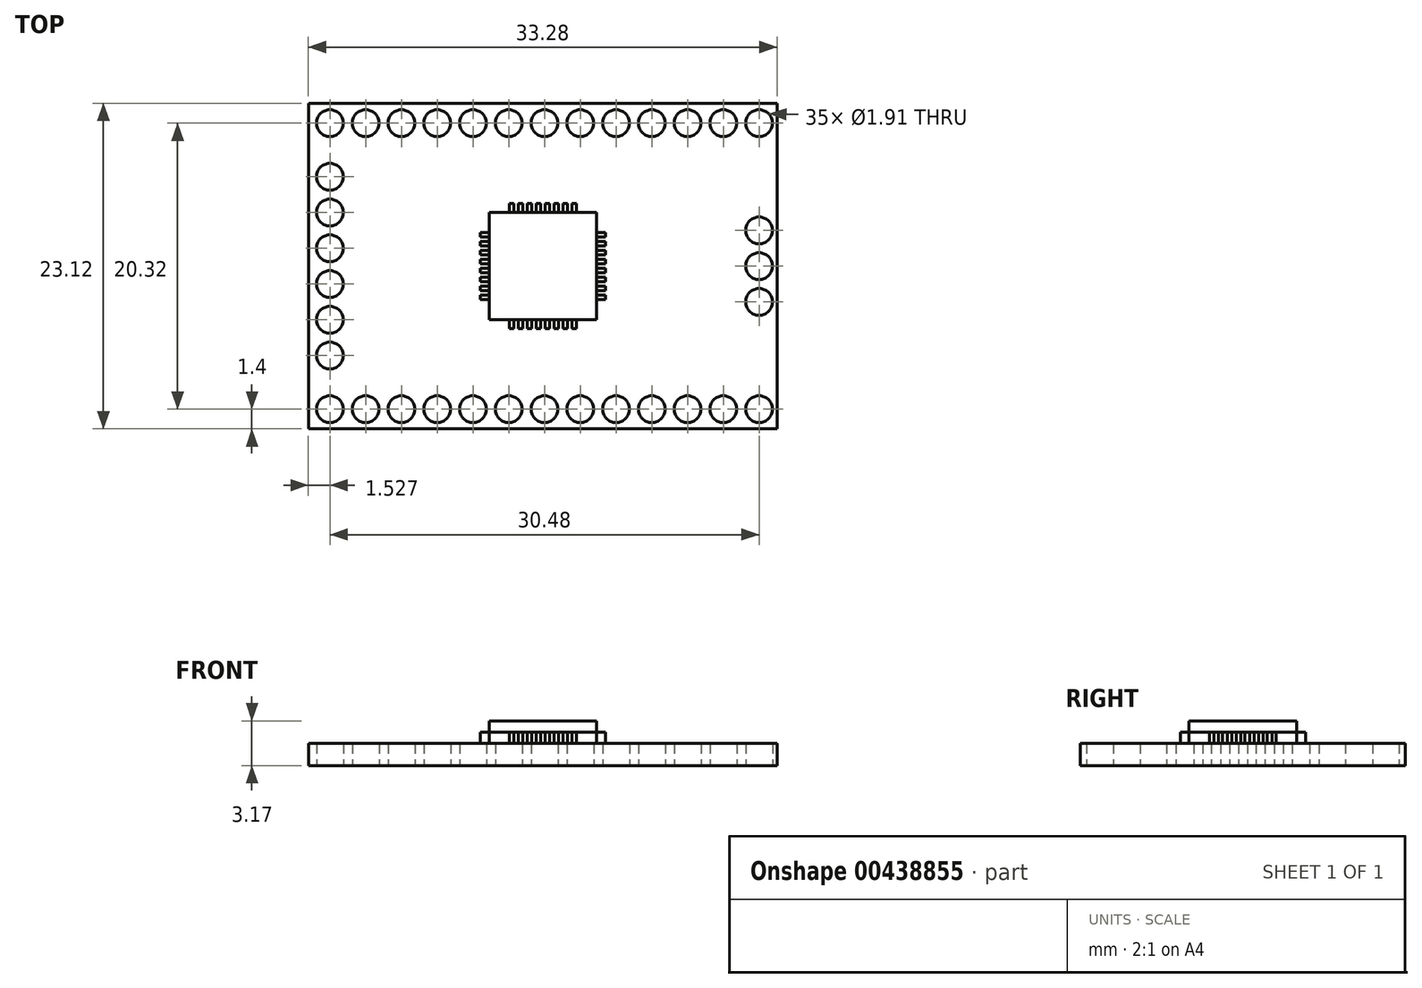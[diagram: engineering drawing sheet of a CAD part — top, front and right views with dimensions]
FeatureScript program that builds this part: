
annotation { "Feature Type Name" : "Feature", "Feature Type Description" : "" }
export const myFeature = defineFeature(function(context is Context, id is Id, definition is map)
    precondition{}
    {
        {
            var Q0;
            Q0=qCreatedBy(makeId("Top.planeOp"),FACE);
            var sketch = newSketch(context, id + "F0", { "sketchPlane" : qUnion([Q0])});
            skLineSegment(sketch, "E0.bottom", {"start": v(16.64, -11.56) * mm, "end": v(-16.64, -11.56) * mm});
            skLineSegment(sketch, "E0.top", {"start": v(16.64, 11.56) * mm, "end": v(-16.64, 11.56) * mm});
            skLineSegment(sketch, "E0.left", {"start": v(16.64, -11.56) * mm, "end": v(16.64, 11.56) * mm});
            skLineSegment(sketch, "E0.right", {"start": v(-16.64, -11.56) * mm, "end": v(-16.64, 11.56) * mm});
            skPoint(sketch, "E0.middle", {"position": v(0, 0) * mm});
            skCircle(sketch, "E1", {"center": v(15.37, -10.16) * mm, "radius": 0.95 * mm});
            skCircle(sketch, "E2", {"center": v(15.37, 10.16) * mm, "radius": 0.95 * mm});
            skLineSegment(sketch, "E3", {"start": v(15.37, -10.16) * mm, "end": v(15.37, 10.16) * mm, "construction": true});
            skPoint(sketch, "E4", {"position": v(15.37, 0) * mm});
            skCircle(sketch, "E5.1.0.0", {"center": v(12.83, -10.16) * mm, "radius": 0.95 * mm});
            skCircle(sketch, "E5.1.0.1", {"center": v(12.83, 10.16) * mm, "radius": 0.95 * mm});
            skCircle(sketch, "E5.2.0.0", {"center": v(10.29, -10.16) * mm, "radius": 0.95 * mm});
            skCircle(sketch, "E5.2.0.1", {"center": v(10.29, 10.16) * mm, "radius": 0.95 * mm});
            skCircle(sketch, "E5.3.0.0", {"center": v(7.75, -10.16) * mm, "radius": 0.95 * mm});
            skCircle(sketch, "E5.3.0.1", {"center": v(7.75, 10.16) * mm, "radius": 0.95 * mm});
            skCircle(sketch, "E5.4.0.0", {"center": v(5.2, -10.16) * mm, "radius": 0.95 * mm});
            skCircle(sketch, "E5.4.0.1", {"center": v(5.2, 10.16) * mm, "radius": 0.95 * mm});
            skCircle(sketch, "E5.5.0.0", {"center": v(2.67, -10.16) * mm, "radius": 0.95 * mm});
            skCircle(sketch, "E5.5.0.1", {"center": v(2.67, 10.16) * mm, "radius": 0.95 * mm});
            skCircle(sketch, "E5.6.0.0", {"center": v(0.13, -10.16) * mm, "radius": 0.95 * mm});
            skCircle(sketch, "E5.6.0.1", {"center": v(0.13, 10.16) * mm, "radius": 0.95 * mm});
            skCircle(sketch, "E5.7.0.0", {"center": v(-2.41, -10.16) * mm, "radius": 0.95 * mm});
            skCircle(sketch, "E5.7.0.1", {"center": v(-2.41, 10.16) * mm, "radius": 0.95 * mm});
            skCircle(sketch, "E5.8.0.0", {"center": v(-4.95, -10.16) * mm, "radius": 0.95 * mm});
            skCircle(sketch, "E5.8.0.1", {"center": v(-4.95, 10.16) * mm, "radius": 0.95 * mm});
            skCircle(sketch, "E5.9.0.0", {"center": v(-7.5, -10.16) * mm, "radius": 0.95 * mm});
            skCircle(sketch, "E5.9.0.1", {"center": v(-7.5, 10.16) * mm, "radius": 0.95 * mm});
            skCircle(sketch, "E5.10.0.0", {"center": v(-10.03, -10.16) * mm, "radius": 0.95 * mm});
            skCircle(sketch, "E5.10.0.1", {"center": v(-10.03, 10.16) * mm, "radius": 0.95 * mm});
            skCircle(sketch, "E5.11.0.0", {"center": v(-12.57, -10.16) * mm, "radius": 0.95 * mm});
            skCircle(sketch, "E5.11.0.1", {"center": v(-12.57, 10.16) * mm, "radius": 0.95 * mm});
            skCircle(sketch, "E5.12.0.0", {"center": v(-15.11, -10.16) * mm, "radius": 0.95 * mm});
            skCircle(sketch, "E5.12.0.1", {"center": v(-15.11, 10.16) * mm, "radius": 0.95 * mm});
            skLineSegment(sketch, "E5.direction1", {"start": v(15.37, -10.16) * mm, "end": v(12.83, -10.16) * mm, "construction": true});
            skCircle(sketch, "E6", {"center": v(15.37, 0) * mm, "radius": 0.95 * mm});
            skLineSegment(sketch, "E7.direction1", {"start": v(15.37, 0) * mm, "end": v(40.77, 0) * mm, "construction": true});
            skLineSegment(sketch, "E7.direction2", {"start": v(15.37, 0) * mm, "end": v(15.37, 2.54) * mm, "construction": true});
            skLineSegment(sketch, "E8", {"start": v(-15.11, 10.16) * mm, "end": v(-15.11, -10.16) * mm, "construction": true});
            skCircle(sketch, "E9", {"center": v(-15.11, -1.27) * mm, "radius": 0.95 * mm});
            skCircle(sketch, "E10.0.0.1", {"center": v(15.37, 2.54) * mm, "radius": 0.95 * mm});
            skCircle(sketch, "E11.0.1.0", {"center": v(-15.11, -3.81) * mm, "radius": 0.95 * mm});
            skCircle(sketch, "E11.0.2.0", {"center": v(-15.11, -6.35) * mm, "radius": 0.95 * mm});
            skLineSegment(sketch, "E11.direction1", {"start": v(-15.11, -1.27) * mm, "end": v(-8.5, -1.27) * mm, "construction": true});
            skLineSegment(sketch, "E11.direction2", {"start": v(-15.11, -1.27) * mm, "end": v(-15.11, -3.81) * mm, "construction": true});
            skCircle(sketch, "E12.MirrorC", {"center": v(15.37, -2.54) * mm, "radius": 0.95 * mm});
            skCircle(sketch, "E13.MirrorC", {"center": v(-15.11, 1.27) * mm, "radius": 0.95 * mm});
            skCircle(sketch, "E14.MirrorC", {"center": v(-15.11, 3.81) * mm, "radius": 0.95 * mm});
            skCircle(sketch, "E15.MirrorC", {"center": v(-15.11, 6.35) * mm, "radius": 0.95 * mm});
            skSolve(sketch);
        }
        {
            var Q0;
            Q0=qSketchRegion(id+"F0",true);
            extrude(context, id + "F1", {"entities" : qUnion([Q0]), "depth" : 1.59 * mm});
        }
        {
            var Q0;
            Q0=makeQuery(id+"F1.opExtrude","CAP_FACE",FACE,{"disambiguationData":[OSD([sQuery(id+"F0.wireOp",EDGE,"E0.bottom"),sQuery(id+"F0.wireOp",EDGE,"E0.top"),sQuery(id+"F0.wireOp",EDGE,"E0.left"),sQuery(id+"F0.wireOp",EDGE,"E0.right"),sQuery(id+"F0.wireOp",EDGE,"E1"),sQuery(id+"F0.wireOp",EDGE,"E2"),sQuery(id+"F0.wireOp",EDGE,"E5.1.0.0"),sQuery(id+"F0.wireOp",EDGE,"E5.1.0.1"),sQuery(id+"F0.wireOp",EDGE,"E5.2.0.0"),sQuery(id+"F0.wireOp",EDGE,"E5.2.0.1"),sQuery(id+"F0.wireOp",EDGE,"E5.3.0.0"),sQuery(id+"F0.wireOp",EDGE,"E5.3.0.1"),sQuery(id+"F0.wireOp",EDGE,"E5.4.0.0"),sQuery(id+"F0.wireOp",EDGE,"E5.4.0.1"),sQuery(id+"F0.wireOp",EDGE,"E5.5.0.0"),sQuery(id+"F0.wireOp",EDGE,"E5.5.0.1"),sQuery(id+"F0.wireOp",EDGE,"E5.6.0.0"),sQuery(id+"F0.wireOp",EDGE,"E5.6.0.1"),sQuery(id+"F0.wireOp",EDGE,"E5.7.0.0"),sQuery(id+"F0.wireOp",EDGE,"E5.7.0.1"),sQuery(id+"F0.wireOp",EDGE,"E5.8.0.0"),sQuery(id+"F0.wireOp",EDGE,"E5.8.0.1"),sQuery(id+"F0.wireOp",EDGE,"E5.9.0.0"),sQuery(id+"F0.wireOp",EDGE,"E5.9.0.1"),sQuery(id+"F0.wireOp",EDGE,"E5.10.0.0"),sQuery(id+"F0.wireOp",EDGE,"E5.10.0.1"),sQuery(id+"F0.wireOp",EDGE,"E5.11.0.0"),sQuery(id+"F0.wireOp",EDGE,"E5.11.0.1"),sQuery(id+"F0.wireOp",EDGE,"E5.12.0.0"),sQuery(id+"F0.wireOp",EDGE,"E5.12.0.1"),sQuery(id+"F0.wireOp",EDGE,"E6"),sQuery(id+"F0.wireOp",EDGE,"E9"),sQuery(id+"F0.wireOp",EDGE,"E10.0.0.1"),sQuery(id+"F0.wireOp",EDGE,"E11.0.1.0"),sQuery(id+"F0.wireOp",EDGE,"E11.0.2.0"),sQuery(id+"F0.wireOp",EDGE,"E12.MirrorC"),sQuery(id+"F0.wireOp",EDGE,"E13.MirrorC"),sQuery(id+"F0.wireOp",EDGE,"E14.MirrorC"),sQuery(id+"F0.wireOp",EDGE,"E15.MirrorC")])],"isStart":false});
            var sketch = newSketch(context, id + "F2", { "sketchPlane" : qUnion([Q0])});
            skLineSegment(sketch, "E16.bottom", {"start": v(3.81, -3.8) * mm, "end": v(-3.81, -3.81) * mm});
            skLineSegment(sketch, "E16.top", {"start": v(3.81, 3.81) * mm, "end": v(-3.81, 3.81) * mm});
            skLineSegment(sketch, "E16.left", {"start": v(3.8, -3.81) * mm, "end": v(3.81, 3.81) * mm});
            skLineSegment(sketch, "E16.right", {"start": v(-3.81, -3.81) * mm, "end": v(-3.8, 3.8) * mm});
            skPoint(sketch, "E16.middle", {"position": v(0, 0) * mm});
            skLineSegment(sketch, "E17.bottom", {"start": v(-0.16, -4.45) * mm, "end": v(-0.48, -4.45) * mm});
            skLineSegment(sketch, "E17.top", {"start": v(-0.16, -3.18) * mm, "end": v(-0.48, -3.18) * mm});
            skLineSegment(sketch, "E17.left", {"start": v(-0.16, -4.45) * mm, "end": v(-0.16, -3.18) * mm});
            skLineSegment(sketch, "E17.right", {"start": v(-0.48, -4.45) * mm, "end": v(-0.48, -3.18) * mm});
            skPoint(sketch, "E17.middle", {"position": v(-0.32, -3.81) * mm});
            skLineSegment(sketch, "E18", {"start": v(0, 3.81) * mm, "end": v(0, -3.81) * mm, "construction": true});
            skLineSegment(sketch, "E19.1.0.0", {"start": v(-0.8, -4.45) * mm, "end": v(-1.11, -4.45) * mm});
            skLineSegment(sketch, "E19.1.0.1", {"start": v(-0.8, -3.18) * mm, "end": v(-1.11, -3.18) * mm});
            skLineSegment(sketch, "E19.1.0.2", {"start": v(-0.8, -4.45) * mm, "end": v(-0.8, -3.18) * mm});
            skPoint(sketch, "E19.1.0.3", {"position": v(-0.95, -3.81) * mm});
            skLineSegment(sketch, "E19.1.0.4", {"start": v(-1.11, -4.45) * mm, "end": v(-1.11, -3.18) * mm});
            skLineSegment(sketch, "E19.2.0.0", {"start": v(-1.43, -4.45) * mm, "end": v(-1.75, -4.45) * mm});
            skLineSegment(sketch, "E19.2.0.1", {"start": v(-1.43, -3.18) * mm, "end": v(-1.75, -3.18) * mm});
            skLineSegment(sketch, "E19.2.0.2", {"start": v(-1.43, -4.45) * mm, "end": v(-1.43, -3.18) * mm});
            skPoint(sketch, "E19.2.0.3", {"position": v(-1.59, -3.81) * mm});
            skLineSegment(sketch, "E19.2.0.4", {"start": v(-1.75, -4.45) * mm, "end": v(-1.75, -3.18) * mm});
            skLineSegment(sketch, "E19.3.0.0", {"start": v(-2.06, -4.45) * mm, "end": v(-2.38, -4.45) * mm});
            skLineSegment(sketch, "E19.3.0.1", {"start": v(-2.06, -3.18) * mm, "end": v(-2.38, -3.18) * mm});
            skLineSegment(sketch, "E19.3.0.2", {"start": v(-2.06, -4.45) * mm, "end": v(-2.06, -3.18) * mm});
            skPoint(sketch, "E19.3.0.3", {"position": v(-2.22, -3.81) * mm});
            skLineSegment(sketch, "E19.3.0.4", {"start": v(-2.38, -4.45) * mm, "end": v(-2.38, -3.18) * mm});
            skLineSegment(sketch, "E19.direction1", {"start": v(-0.48, -4.45) * mm, "end": v(-1.11, -4.45) * mm, "construction": true});
            skLineSegment(sketch, "E20.MirrorCS", {"start": v(0.8, -4.45) * mm, "end": v(1.11, -4.45) * mm});
            skLineSegment(sketch, "E21.MirrorCS", {"start": v(2.06, -3.18) * mm, "end": v(2.38, -3.18) * mm});
            skLineSegment(sketch, "E22.MirrorCS", {"start": v(2.06, -4.45) * mm, "end": v(2.38, -4.45) * mm});
            skLineSegment(sketch, "E23.MirrorCS", {"start": v(0.16, -4.45) * mm, "end": v(0.48, -4.45) * mm});
            skPoint(sketch, "E24.MirrorP", {"position": v(1.59, -3.81) * mm});
            skLineSegment(sketch, "E25.MirrorCS", {"start": v(1.43, -4.45) * mm, "end": v(1.75, -4.45) * mm});
            skLineSegment(sketch, "E26.MirrorCS", {"start": v(2.06, -4.45) * mm, "end": v(2.06, -3.18) * mm});
            skLineSegment(sketch, "E27.MirrorCS", {"start": v(0.16, -3.18) * mm, "end": v(0.48, -3.18) * mm});
            skPoint(sketch, "E28.MirrorP", {"position": v(2.22, -3.81) * mm});
            skLineSegment(sketch, "E29.MirrorCS", {"start": v(2.38, -4.45) * mm, "end": v(2.38, -3.18) * mm});
            skLineSegment(sketch, "E30.MirrorCS", {"start": v(0.16, -4.45) * mm, "end": v(0.16, -3.18) * mm});
            skLineSegment(sketch, "E31.MirrorCS", {"start": v(0.48, -4.45) * mm, "end": v(0.48, -3.18) * mm});
            skPoint(sketch, "E32.MirrorP", {"position": v(0.95, -3.81) * mm});
            skLineSegment(sketch, "E33.MirrorCS", {"start": v(1.43, -4.45) * mm, "end": v(1.43, -3.18) * mm});
            skLineSegment(sketch, "E34.MirrorCS", {"start": v(1.75, -4.45) * mm, "end": v(1.75, -3.18) * mm});
            skPoint(sketch, "E35.MirrorP", {"position": v(0.32, -3.81) * mm});
            skLineSegment(sketch, "E36.MirrorCS", {"start": v(1.11, -4.45) * mm, "end": v(1.11, -3.18) * mm});
            skLineSegment(sketch, "E37.MirrorCS", {"start": v(1.43, -3.18) * mm, "end": v(1.75, -3.18) * mm});
            skLineSegment(sketch, "E38.MirrorCS", {"start": v(0.8, -3.18) * mm, "end": v(1.11, -3.18) * mm});
            skLineSegment(sketch, "E39.MirrorCS", {"start": v(0.8, -4.45) * mm, "end": v(0.8, -3.18) * mm});
            skLineSegment(sketch, "E40.1.0", {"start": v(4.45, 1.43) * mm, "end": v(3.18, 1.43) * mm});
            skLineSegment(sketch, "E40.1.1", {"start": v(4.45, -2.06) * mm, "end": v(3.18, -2.06) * mm});
            skPoint(sketch, "E40.1.2", {"position": v(3.81, -1.59) * mm});
            skLineSegment(sketch, "E40.1.3", {"start": v(4.45, -0.48) * mm, "end": v(3.18, -0.48) * mm});
            skLineSegment(sketch, "E40.1.4", {"start": v(4.45, 2.06) * mm, "end": v(3.18, 2.06) * mm});
            skLineSegment(sketch, "E40.1.5", {"start": v(4.45, 2.38) * mm, "end": v(3.18, 2.38) * mm});
            skLineSegment(sketch, "E40.1.6", {"start": v(4.45, -2.38) * mm, "end": v(3.18, -2.38) * mm});
            skPoint(sketch, "E40.1.7", {"position": v(3.81, 1.59) * mm});
            skPoint(sketch, "E40.1.8", {"position": v(3.81, 2.22) * mm});
            skPoint(sketch, "E40.1.9", {"position": v(3.81, 0.32) * mm});
            skPoint(sketch, "E40.1.10", {"position": v(3.81, -0.32) * mm});
            skLineSegment(sketch, "E40.1.11", {"start": v(4.45, 0.8) * mm, "end": v(3.18, 0.8) * mm});
            skLineSegment(sketch, "E40.1.12", {"start": v(4.45, 0.16) * mm, "end": v(3.18, 0.16) * mm});
            skLineSegment(sketch, "E40.1.13", {"start": v(4.45, -0.16) * mm, "end": v(3.18, -0.16) * mm});
            skLineSegment(sketch, "E40.1.14", {"start": v(4.45, -0.8) * mm, "end": v(3.18, -0.8) * mm});
            skLineSegment(sketch, "E40.1.15", {"start": v(4.45, 0.48) * mm, "end": v(3.18, 0.48) * mm});
            skLineSegment(sketch, "E40.1.16", {"start": v(4.45, -1.11) * mm, "end": v(3.18, -1.11) * mm});
            skPoint(sketch, "E40.1.17", {"position": v(3.81, -2.22) * mm});
            skLineSegment(sketch, "E40.1.18", {"start": v(4.45, 1.11) * mm, "end": v(3.18, 1.11) * mm});
            skLineSegment(sketch, "E40.1.19", {"start": v(4.45, 1.75) * mm, "end": v(3.18, 1.75) * mm});
            skLineSegment(sketch, "E40.1.20", {"start": v(4.45, -1.43) * mm, "end": v(3.18, -1.43) * mm});
            skPoint(sketch, "E40.1.21", {"position": v(3.81, 0.95) * mm});
            skPoint(sketch, "E40.1.22", {"position": v(3.81, -0.95) * mm});
            skLineSegment(sketch, "E40.1.23", {"start": v(4.45, -1.75) * mm, "end": v(3.18, -1.75) * mm});
            skLineSegment(sketch, "E40.1.24", {"start": v(3.18, 0.8) * mm, "end": v(3.18, 1.11) * mm});
            skLineSegment(sketch, "E40.1.25", {"start": v(4.45, -0.8) * mm, "end": v(4.45, -1.11) * mm});
            skLineSegment(sketch, "E40.1.26", {"start": v(3.18, -1.43) * mm, "end": v(3.18, -1.75) * mm});
            skLineSegment(sketch, "E40.1.27", {"start": v(3.18, -0.16) * mm, "end": v(3.18, -0.48) * mm});
            skLineSegment(sketch, "E40.1.28", {"start": v(3.18, 0.16) * mm, "end": v(3.18, 0.48) * mm});
            skLineSegment(sketch, "E40.1.29", {"start": v(3.18, -0.8) * mm, "end": v(3.18, -1.11) * mm});
            skLineSegment(sketch, "E40.1.30", {"start": v(4.45, 0.16) * mm, "end": v(4.45, 0.48) * mm});
            skLineSegment(sketch, "E40.1.31", {"start": v(4.45, 0.8) * mm, "end": v(4.45, 1.11) * mm});
            skLineSegment(sketch, "E40.1.32", {"start": v(4.45, -1.43) * mm, "end": v(4.45, -1.75) * mm});
            skLineSegment(sketch, "E40.1.33", {"start": v(3.18, 2.06) * mm, "end": v(3.18, 2.38) * mm});
            skLineSegment(sketch, "E40.1.34", {"start": v(4.45, 2.06) * mm, "end": v(4.45, 2.38) * mm});
            skLineSegment(sketch, "E40.1.35", {"start": v(3.18, 1.43) * mm, "end": v(3.18, 1.75) * mm});
            skLineSegment(sketch, "E40.1.36", {"start": v(4.45, 1.43) * mm, "end": v(4.45, 1.75) * mm});
            skLineSegment(sketch, "E40.1.37", {"start": v(4.45, -2.06) * mm, "end": v(4.45, -2.38) * mm});
            skLineSegment(sketch, "E40.1.38", {"start": v(3.18, -2.06) * mm, "end": v(3.18, -2.38) * mm});
            skLineSegment(sketch, "E40.1.39", {"start": v(4.45, -0.16) * mm, "end": v(4.45, -0.48) * mm});
            skLineSegment(sketch, "E40.2.0", {"start": v(-1.43, 4.45) * mm, "end": v(-1.43, 3.18) * mm});
            skLineSegment(sketch, "E40.2.1", {"start": v(2.06, 4.45) * mm, "end": v(2.06, 3.18) * mm});
            skPoint(sketch, "E40.2.2", {"position": v(1.59, 3.81) * mm});
            skLineSegment(sketch, "E40.2.3", {"start": v(0.48, 4.45) * mm, "end": v(0.48, 3.18) * mm});
            skLineSegment(sketch, "E40.2.4", {"start": v(-2.06, 4.45) * mm, "end": v(-2.06, 3.18) * mm});
            skLineSegment(sketch, "E40.2.5", {"start": v(-2.38, 4.45) * mm, "end": v(-2.38, 3.18) * mm});
            skLineSegment(sketch, "E40.2.6", {"start": v(2.38, 4.45) * mm, "end": v(2.38, 3.18) * mm});
            skPoint(sketch, "E40.2.7", {"position": v(-1.59, 3.81) * mm});
            skPoint(sketch, "E40.2.8", {"position": v(-2.22, 3.81) * mm});
            skPoint(sketch, "E40.2.9", {"position": v(-0.32, 3.81) * mm});
            skPoint(sketch, "E40.2.10", {"position": v(0.32, 3.81) * mm});
            skLineSegment(sketch, "E40.2.11", {"start": v(-0.8, 4.45) * mm, "end": v(-0.8, 3.18) * mm});
            skLineSegment(sketch, "E40.2.12", {"start": v(-0.16, 4.45) * mm, "end": v(-0.16, 3.18) * mm});
            skLineSegment(sketch, "E40.2.13", {"start": v(0.16, 4.45) * mm, "end": v(0.16, 3.18) * mm});
            skLineSegment(sketch, "E40.2.14", {"start": v(0.8, 4.45) * mm, "end": v(0.8, 3.18) * mm});
            skLineSegment(sketch, "E40.2.15", {"start": v(-0.48, 4.45) * mm, "end": v(-0.48, 3.18) * mm});
            skLineSegment(sketch, "E40.2.16", {"start": v(1.11, 4.45) * mm, "end": v(1.11, 3.18) * mm});
            skPoint(sketch, "E40.2.17", {"position": v(2.22, 3.81) * mm});
            skLineSegment(sketch, "E40.2.18", {"start": v(-1.11, 4.45) * mm, "end": v(-1.11, 3.18) * mm});
            skLineSegment(sketch, "E40.2.19", {"start": v(-1.75, 4.45) * mm, "end": v(-1.75, 3.18) * mm});
            skLineSegment(sketch, "E40.2.20", {"start": v(1.43, 4.45) * mm, "end": v(1.43, 3.18) * mm});
            skPoint(sketch, "E40.2.21", {"position": v(-0.95, 3.81) * mm});
            skPoint(sketch, "E40.2.22", {"position": v(0.95, 3.81) * mm});
            skLineSegment(sketch, "E40.2.23", {"start": v(1.75, 4.45) * mm, "end": v(1.75, 3.18) * mm});
            skLineSegment(sketch, "E40.2.24", {"start": v(-0.8, 3.18) * mm, "end": v(-1.11, 3.18) * mm});
            skLineSegment(sketch, "E40.2.25", {"start": v(0.8, 4.45) * mm, "end": v(1.11, 4.45) * mm});
            skLineSegment(sketch, "E40.2.26", {"start": v(1.43, 3.18) * mm, "end": v(1.75, 3.18) * mm});
            skLineSegment(sketch, "E40.2.27", {"start": v(0.16, 3.18) * mm, "end": v(0.48, 3.18) * mm});
            skLineSegment(sketch, "E40.2.28", {"start": v(-0.16, 3.18) * mm, "end": v(-0.48, 3.18) * mm});
            skLineSegment(sketch, "E40.2.29", {"start": v(0.8, 3.18) * mm, "end": v(1.11, 3.18) * mm});
            skLineSegment(sketch, "E40.2.30", {"start": v(-0.16, 4.45) * mm, "end": v(-0.48, 4.45) * mm});
            skLineSegment(sketch, "E40.2.31", {"start": v(-0.8, 4.45) * mm, "end": v(-1.11, 4.45) * mm});
            skLineSegment(sketch, "E40.2.32", {"start": v(1.43, 4.45) * mm, "end": v(1.75, 4.45) * mm});
            skLineSegment(sketch, "E40.2.33", {"start": v(-2.06, 3.18) * mm, "end": v(-2.38, 3.18) * mm});
            skLineSegment(sketch, "E40.2.34", {"start": v(-2.06, 4.45) * mm, "end": v(-2.38, 4.45) * mm});
            skLineSegment(sketch, "E40.2.35", {"start": v(-1.43, 3.18) * mm, "end": v(-1.75, 3.18) * mm});
            skLineSegment(sketch, "E40.2.36", {"start": v(-1.43, 4.45) * mm, "end": v(-1.75, 4.45) * mm});
            skLineSegment(sketch, "E40.2.37", {"start": v(2.06, 4.45) * mm, "end": v(2.38, 4.45) * mm});
            skLineSegment(sketch, "E40.2.38", {"start": v(2.06, 3.18) * mm, "end": v(2.38, 3.18) * mm});
            skLineSegment(sketch, "E40.2.39", {"start": v(0.16, 4.45) * mm, "end": v(0.48, 4.45) * mm});
            skLineSegment(sketch, "E40.3.0", {"start": v(-4.45, -1.43) * mm, "end": v(-3.18, -1.43) * mm});
            skLineSegment(sketch, "E40.3.1", {"start": v(-4.45, 2.06) * mm, "end": v(-3.18, 2.06) * mm});
            skPoint(sketch, "E40.3.2", {"position": v(-3.81, 1.59) * mm});
            skLineSegment(sketch, "E40.3.3", {"start": v(-4.45, 0.48) * mm, "end": v(-3.18, 0.48) * mm});
            skLineSegment(sketch, "E40.3.4", {"start": v(-4.45, -2.06) * mm, "end": v(-3.18, -2.06) * mm});
            skLineSegment(sketch, "E40.3.5", {"start": v(-4.45, -2.38) * mm, "end": v(-3.18, -2.38) * mm});
            skLineSegment(sketch, "E40.3.6", {"start": v(-4.45, 2.38) * mm, "end": v(-3.18, 2.38) * mm});
            skPoint(sketch, "E40.3.7", {"position": v(-3.81, -1.59) * mm});
            skPoint(sketch, "E40.3.8", {"position": v(-3.81, -2.22) * mm});
            skPoint(sketch, "E40.3.9", {"position": v(-3.81, -0.32) * mm});
            skPoint(sketch, "E40.3.10", {"position": v(-3.81, 0.32) * mm});
            skLineSegment(sketch, "E40.3.11", {"start": v(-4.45, -0.8) * mm, "end": v(-3.18, -0.8) * mm});
            skLineSegment(sketch, "E40.3.12", {"start": v(-4.45, -0.16) * mm, "end": v(-3.18, -0.16) * mm});
            skLineSegment(sketch, "E40.3.13", {"start": v(-4.45, 0.16) * mm, "end": v(-3.18, 0.16) * mm});
            skLineSegment(sketch, "E40.3.14", {"start": v(-4.45, 0.8) * mm, "end": v(-3.18, 0.8) * mm});
            skLineSegment(sketch, "E40.3.15", {"start": v(-4.45, -0.48) * mm, "end": v(-3.18, -0.48) * mm});
            skLineSegment(sketch, "E40.3.16", {"start": v(-4.45, 1.11) * mm, "end": v(-3.18, 1.11) * mm});
            skPoint(sketch, "E40.3.17", {"position": v(-3.81, 2.22) * mm});
            skLineSegment(sketch, "E40.3.18", {"start": v(-4.45, -1.11) * mm, "end": v(-3.18, -1.11) * mm});
            skLineSegment(sketch, "E40.3.19", {"start": v(-4.45, -1.75) * mm, "end": v(-3.18, -1.75) * mm});
            skLineSegment(sketch, "E40.3.20", {"start": v(-4.45, 1.43) * mm, "end": v(-3.18, 1.43) * mm});
            skPoint(sketch, "E40.3.21", {"position": v(-3.81, -0.95) * mm});
            skPoint(sketch, "E40.3.22", {"position": v(-3.81, 0.95) * mm});
            skLineSegment(sketch, "E40.3.23", {"start": v(-4.45, 1.75) * mm, "end": v(-3.18, 1.75) * mm});
            skLineSegment(sketch, "E40.3.24", {"start": v(-3.18, -0.8) * mm, "end": v(-3.18, -1.11) * mm});
            skLineSegment(sketch, "E40.3.25", {"start": v(-4.45, 0.8) * mm, "end": v(-4.45, 1.11) * mm});
            skLineSegment(sketch, "E40.3.26", {"start": v(-3.18, 1.43) * mm, "end": v(-3.18, 1.75) * mm});
            skLineSegment(sketch, "E40.3.27", {"start": v(-3.18, 0.16) * mm, "end": v(-3.18, 0.48) * mm});
            skLineSegment(sketch, "E40.3.28", {"start": v(-3.18, -0.16) * mm, "end": v(-3.18, -0.48) * mm});
            skLineSegment(sketch, "E40.3.29", {"start": v(-3.18, 0.8) * mm, "end": v(-3.18, 1.11) * mm});
            skLineSegment(sketch, "E40.3.30", {"start": v(-4.45, -0.16) * mm, "end": v(-4.45, -0.48) * mm});
            skLineSegment(sketch, "E40.3.31", {"start": v(-4.45, -0.8) * mm, "end": v(-4.45, -1.11) * mm});
            skLineSegment(sketch, "E40.3.32", {"start": v(-4.45, 1.43) * mm, "end": v(-4.45, 1.75) * mm});
            skLineSegment(sketch, "E40.3.33", {"start": v(-3.18, -2.06) * mm, "end": v(-3.18, -2.38) * mm});
            skLineSegment(sketch, "E40.3.34", {"start": v(-4.45, -2.06) * mm, "end": v(-4.45, -2.38) * mm});
            skLineSegment(sketch, "E40.3.35", {"start": v(-3.18, -1.43) * mm, "end": v(-3.18, -1.75) * mm});
            skLineSegment(sketch, "E40.3.36", {"start": v(-4.45, -1.43) * mm, "end": v(-4.45, -1.75) * mm});
            skLineSegment(sketch, "E40.3.37", {"start": v(-4.45, 2.06) * mm, "end": v(-4.45, 2.38) * mm});
            skLineSegment(sketch, "E40.3.38", {"start": v(-3.18, 2.06) * mm, "end": v(-3.18, 2.38) * mm});
            skLineSegment(sketch, "E40.3.39", {"start": v(-4.45, 0.16) * mm, "end": v(-4.45, 0.48) * mm});
            skSolve(sketch);
        }
        {
            var Q0;
            Q0=qSketchRegion(id+"F2",true);
            extrude(context, id + "F3", {"entities" : qUnion([Q0]), "depth" : 0.8 * mm});
        }
        {
            var Q0;
            Q0=makeQuery(id+"F3.opExtrude","CAP_FACE",FACE,{"disambiguationData":[OSD([sQuery(id+"F2.wireOp",EDGE,"E16.bottom"),sQuery(id+"F2.wireOp",EDGE,"E16.top"),sQuery(id+"F2.wireOp",EDGE,"E16.left"),sQuery(id+"F2.wireOp",EDGE,"E16.right"),sQuery(id+"F2.wireOp",EDGE,"E17.bottom"),sQuery(id+"F2.wireOp",EDGE,"E17.left"),sQuery(id+"F2.wireOp",EDGE,"E17.right"),sQuery(id+"F2.wireOp",EDGE,"E19.1.0.0"),sQuery(id+"F2.wireOp",EDGE,"E19.1.0.2"),sQuery(id+"F2.wireOp",EDGE,"E19.1.0.4"),sQuery(id+"F2.wireOp",EDGE,"E19.2.0.0"),sQuery(id+"F2.wireOp",EDGE,"E19.2.0.2"),sQuery(id+"F2.wireOp",EDGE,"E19.2.0.4"),sQuery(id+"F2.wireOp",EDGE,"E19.3.0.0"),sQuery(id+"F2.wireOp",EDGE,"E19.3.0.2"),sQuery(id+"F2.wireOp",EDGE,"E19.3.0.4"),sQuery(id+"F2.wireOp",EDGE,"E20.MirrorCS"),sQuery(id+"F2.wireOp",EDGE,"E22.MirrorCS"),sQuery(id+"F2.wireOp",EDGE,"E23.MirrorCS"),sQuery(id+"F2.wireOp",EDGE,"E25.MirrorCS"),sQuery(id+"F2.wireOp",EDGE,"E26.MirrorCS"),sQuery(id+"F2.wireOp",EDGE,"E29.MirrorCS"),sQuery(id+"F2.wireOp",EDGE,"E30.MirrorCS"),sQuery(id+"F2.wireOp",EDGE,"E31.MirrorCS"),sQuery(id+"F2.wireOp",EDGE,"E33.MirrorCS"),sQuery(id+"F2.wireOp",EDGE,"E34.MirrorCS"),sQuery(id+"F2.wireOp",EDGE,"E36.MirrorCS"),sQuery(id+"F2.wireOp",EDGE,"E39.MirrorCS"),sQuery(id+"F2.wireOp",EDGE,"E40.1.0"),sQuery(id+"F2.wireOp",EDGE,"E40.1.1"),sQuery(id+"F2.wireOp",EDGE,"E40.1.3"),sQuery(id+"F2.wireOp",EDGE,"E40.1.4"),sQuery(id+"F2.wireOp",EDGE,"E40.1.5"),sQuery(id+"F2.wireOp",EDGE,"E40.1.6"),sQuery(id+"F2.wireOp",EDGE,"E40.1.11"),sQuery(id+"F2.wireOp",EDGE,"E40.1.12"),sQuery(id+"F2.wireOp",EDGE,"E40.1.13"),sQuery(id+"F2.wireOp",EDGE,"E40.1.14"),sQuery(id+"F2.wireOp",EDGE,"E40.1.15"),sQuery(id+"F2.wireOp",EDGE,"E40.1.16"),sQuery(id+"F2.wireOp",EDGE,"E40.1.18"),sQuery(id+"F2.wireOp",EDGE,"E40.1.19"),sQuery(id+"F2.wireOp",EDGE,"E40.1.20"),sQuery(id+"F2.wireOp",EDGE,"E40.1.23"),sQuery(id+"F2.wireOp",EDGE,"E40.1.25"),sQuery(id+"F2.wireOp",EDGE,"E40.1.30"),sQuery(id+"F2.wireOp",EDGE,"E40.1.31"),sQuery(id+"F2.wireOp",EDGE,"E40.1.32"),sQuery(id+"F2.wireOp",EDGE,"E40.1.34"),sQuery(id+"F2.wireOp",EDGE,"E40.1.36"),sQuery(id+"F2.wireOp",EDGE,"E40.1.37"),sQuery(id+"F2.wireOp",EDGE,"E40.1.39"),sQuery(id+"F2.wireOp",EDGE,"E40.2.0"),sQuery(id+"F2.wireOp",EDGE,"E40.2.1"),sQuery(id+"F2.wireOp",EDGE,"E40.2.3"),sQuery(id+"F2.wireOp",EDGE,"E40.2.4"),sQuery(id+"F2.wireOp",EDGE,"E40.2.5"),sQuery(id+"F2.wireOp",EDGE,"E40.2.6"),sQuery(id+"F2.wireOp",EDGE,"E40.2.11"),sQuery(id+"F2.wireOp",EDGE,"E40.2.12"),sQuery(id+"F2.wireOp",EDGE,"E40.2.13"),sQuery(id+"F2.wireOp",EDGE,"E40.2.14"),sQuery(id+"F2.wireOp",EDGE,"E40.2.15"),sQuery(id+"F2.wireOp",EDGE,"E40.2.16"),sQuery(id+"F2.wireOp",EDGE,"E40.2.18"),sQuery(id+"F2.wireOp",EDGE,"E40.2.19"),sQuery(id+"F2.wireOp",EDGE,"E40.2.20"),sQuery(id+"F2.wireOp",EDGE,"E40.2.23"),sQuery(id+"F2.wireOp",EDGE,"E40.2.25"),sQuery(id+"F2.wireOp",EDGE,"E40.2.30"),sQuery(id+"F2.wireOp",EDGE,"E40.2.31"),sQuery(id+"F2.wireOp",EDGE,"E40.2.32"),sQuery(id+"F2.wireOp",EDGE,"E40.2.34"),sQuery(id+"F2.wireOp",EDGE,"E40.2.36"),sQuery(id+"F2.wireOp",EDGE,"E40.2.37"),sQuery(id+"F2.wireOp",EDGE,"E40.2.39"),sQuery(id+"F2.wireOp",EDGE,"E40.3.0"),sQuery(id+"F2.wireOp",EDGE,"E40.3.1"),sQuery(id+"F2.wireOp",EDGE,"E40.3.3"),sQuery(id+"F2.wireOp",EDGE,"E40.3.4"),sQuery(id+"F2.wireOp",EDGE,"E40.3.5"),sQuery(id+"F2.wireOp",EDGE,"E40.3.6"),sQuery(id+"F2.wireOp",EDGE,"E40.3.11"),sQuery(id+"F2.wireOp",EDGE,"E40.3.12"),sQuery(id+"F2.wireOp",EDGE,"E40.3.13"),sQuery(id+"F2.wireOp",EDGE,"E40.3.14"),sQuery(id+"F2.wireOp",EDGE,"E40.3.15"),sQuery(id+"F2.wireOp",EDGE,"E40.3.16"),sQuery(id+"F2.wireOp",EDGE,"E40.3.18"),sQuery(id+"F2.wireOp",EDGE,"E40.3.19"),sQuery(id+"F2.wireOp",EDGE,"E40.3.20"),sQuery(id+"F2.wireOp",EDGE,"E40.3.23"),sQuery(id+"F2.wireOp",EDGE,"E40.3.25"),sQuery(id+"F2.wireOp",EDGE,"E40.3.30"),sQuery(id+"F2.wireOp",EDGE,"E40.3.31"),sQuery(id+"F2.wireOp",EDGE,"E40.3.32"),sQuery(id+"F2.wireOp",EDGE,"E40.3.34"),sQuery(id+"F2.wireOp",EDGE,"E40.3.36"),sQuery(id+"F2.wireOp",EDGE,"E40.3.37"),sQuery(id+"F2.wireOp",EDGE,"E40.3.39")])],"isStart":false});
            var sketch = newSketch(context, id + "F4", { "sketchPlane" : qUnion([Q0])});
            skLineSegment(sketch, "E41.bottom", {"start": v(3.81, -3.8) * mm, "end": v(-3.81, -3.8) * mm});
            skLineSegment(sketch, "E41.top", {"start": v(3.81, 3.8) * mm, "end": v(-3.81, 3.8) * mm});
            skLineSegment(sketch, "E41.left", {"start": v(3.81, -3.8) * mm, "end": v(3.81, 3.8) * mm});
            skLineSegment(sketch, "E41.right", {"start": v(-3.81, -3.8) * mm, "end": v(-3.81, 3.8) * mm});
            skPoint(sketch, "E41.middle", {"position": v(0, 0) * mm});
            skSolve(sketch);
        }
        {
            var Q0;
            Q0=qSketchRegion(id+"F4",true);
            extrude(context, id + "F5", {"entities" : qUnion([Q0]), "depth" : 0.8 * mm});
        }
    });
